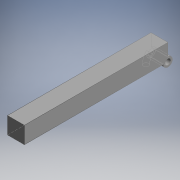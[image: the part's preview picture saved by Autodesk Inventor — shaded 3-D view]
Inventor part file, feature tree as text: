
AUTODESK INVENTOR PART (.ipt)
format: ipt  version: 2018 (Build 220112000, 112)  size: 129,536 bytes
history: native  units: in
note: dims shown in document units (in); Inventor stores cm internally (conversion verified against a paired STEP export)
features: extrude x3, sweep x3, other x1, plane x1, imported_body x1
ambient origin geometry x8: Origin, YZ Plane, XZ Plane, XY Plane, X Axis, Y Axis, Z Axis, Center Point
bodies: Solid1 (feature_tree)
feature tree (9):
  extrude  "Main Body"  TaperAngle=0.0deg  [1 undecoded]
  other  "Hinge Sketch"
  extrude  "Hinge Surround"  Depth=0.1339in
  extrude  "Hinge Hole"  Depth=0.0394in
  plane  "Work Plane1"
  sweep  "Sweep2"
  imported_body  "Base"
  sweep  "Sweep Path"
  sweep  "Sweep Profile"
note: 1 required parameter value undecoded (feature->parameter linkage not recoverable at this tier; creation-order binding heuristic only, values carry confidence <= 0.55)
